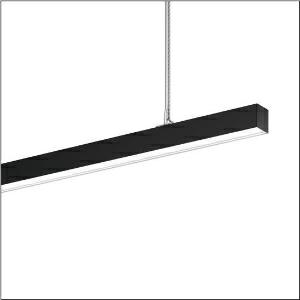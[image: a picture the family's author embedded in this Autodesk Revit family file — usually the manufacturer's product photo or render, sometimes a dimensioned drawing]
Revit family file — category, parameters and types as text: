
# Revit family: silica_r__21_51mx33tbt9b_b685
name_source: partatom
category: Lighting Fixtures
units: mm (PartAtom-declared; Revit-internal decimal feet)

## family parameters
Cut with Voids When Loaded = No
Host = Face
Light Source = No
Part Type = Normal
Room Calculation Point = No
Round Connector Dimension = Use Diameter
Shared = No

## types (1)
- --- (1 x LED, 7170 lm, 67.4 W, 6500K)
    Apparent Load = 67 VA
    CIE Flux Codes = 78 96 99 56 100
    Color Rendering = 80
    Color Temperature = 6500K
    Default Elevation = 1800 mm
    Description = Silica® 21, office luminaire, primary optical cover: prismatic diffuser, of PMMA, CAT 2 (L<= 3000cd/m²), light emission: direct/indirect distribution, primary light characteristic: symmetric, installation type: suspended mounting, LED, rated luminous flux: 7.170lm, luminous efficacy: 101lm/W, light colour: 8tw, colour temperature: 2700..6500K, control gear: ECG DALI, with terminal, 3+2-pole, max. 2.5mm², mains connection: 220..240V, AC, 50/60Hz, rated input power: 70.8W, luminaire housing, of aluminium, jet black (RAL 9005), length: 1.504mm, width: 53mm, height: 53mm, protection rating (complete): IP20, insulation class (complete): insulation class I (protective earthing), certification: CE, permissible operating ambient temperature: 0..+35°C, standard: EN 50419, packaging unit: 1 piece
    Height = 53 mm
    Lamp = 1 x LED
    Lamp Light Flux = 7170 lm
    Lamp Power = 67.4 W
    Lamp count = 1
    Length = 1504 mm
    Luminous efficacy = 106 lm/W
    Manufacturer = Siteco
    ModVariant = No
    Model = 51MX33TBT9B
    Mounting Place = Ceiling
    Mounting Type = Pendant
    Number of Poles = 1
    OnlyDefault = Yes
    Power Factor = 1
    Product Name = Silica® 21
    Product group = office luminaire | ceiling pendant
    ProductGroupID = 902
    Protection Class = Protection class I
    Protection Degree = IP 20
    RLX_Detail_Level = 1
    RLX_Emergency_Light_Flux = 0 lm
    RLX_Emergency_Type = 0
    RLX_Emergency_Type_DB = No
    RlxData = <blob elided: 22945 chars, md5=c0c908bb>
    Socket = socket
    Standby Power = 0 W
    System Light Flux = 7170 lm
    System Power = 67 W
    Type Comments = individual setting
    Type Image = l_1297744.jpg
    URL = http://relux.com
    VarID = @adj_071083
    Voltage = 0 V
    Weight = 0.00 kg
    Width = 53 mm

## geometry (parser evidence)
native form markers: Blend x4, Sweep x12
no freeform markers — native parametric forms only
